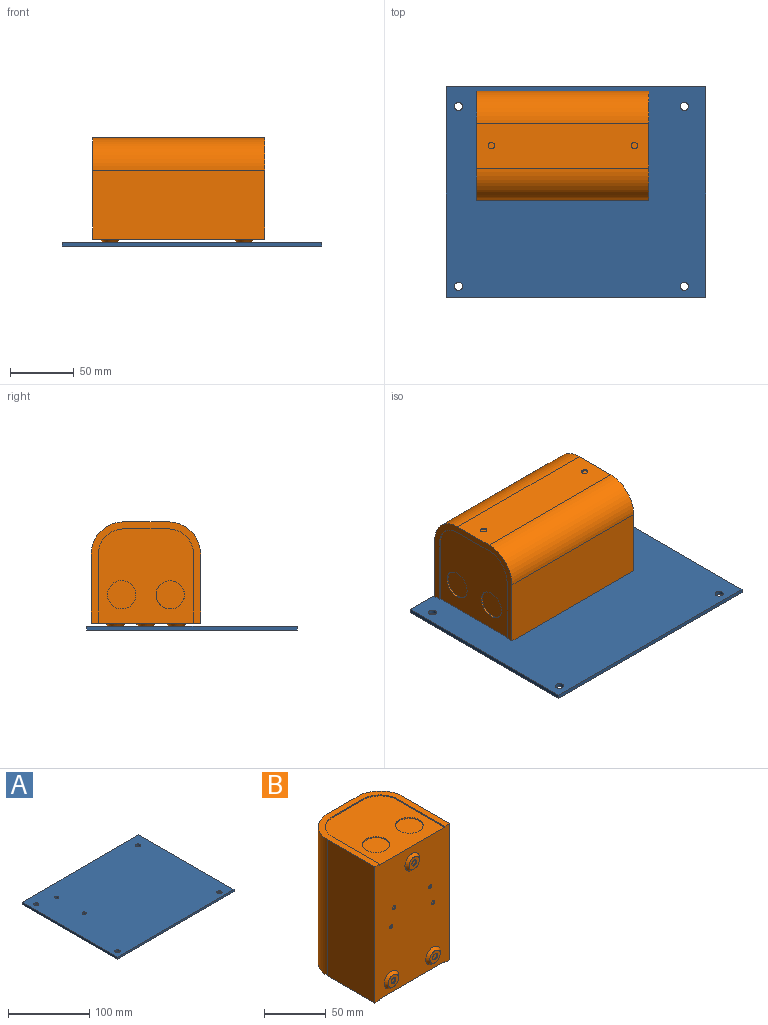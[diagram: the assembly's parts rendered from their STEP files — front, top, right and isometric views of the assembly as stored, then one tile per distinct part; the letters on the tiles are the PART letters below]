
ASSEMBLY  parts=2 mates=1
PART A: 12 faces, bbox 203x165x3.1 mm
  f0: plane 203x3.1mm, normal (0,-1,0), area 629.3mm2, adj f1,f9,f10,f11
  f1: plane 165x3.1mm, normal (1,0,0), area 511.5mm2, adj f0,f2,f10,f11
  f2: plane 203x3.1mm, normal (0,1,0), area 629.3mm2, adj f1,f9,f10,f11
  f3: cylinder r=3.17mm len=6.35mm, axis (0,0,-1), area 61.8mm2, adj f10,f11
  f4: cylinder r=3.17mm len=6.35mm, axis (0,0,-1), area 61.8mm2, adj f10,f11
  f5: cylinder r=3.17mm len=6.35mm, axis (0,0,-1), area 61.8mm2, adj f10,f11
  f6: cylinder r=3.17mm len=6.35mm, axis (0,0,-1), area 61.8mm2, adj f10,f11
  f7: cylinder r=2.5mm len=5mm, axis (0,0,-1), area 48.7mm2, adj f10,f11
  f8: cylinder r=2.5mm len=5mm, axis (0,0,-1), area 48.7mm2, adj f10,f11
  f9: plane 165x3.1mm, normal (-1,0,0), area 511.5mm2, adj f0,f2,f10,f11
  f10: plane 203x165mm, normal (0,0,1), area 33329.1mm2, adj f0,f1,f2,f3,f4,f5,f6,f7
  f11: plane 203x165mm, normal (0,0,-1), area 33329.1mm2, adj f0,f1,f2,f3,f4,f5,f6,f7
PART B: 52 faces, bbox 85.7x81.7x134.9 mm
  f0: plane 85.73x79.38mm, normal (0,0,1), area 1182.2mm2, adj f1,f2,f10,f11,f12,f13,f14,f23
  f1: plane 53.98x1.02mm, normal (-1,0,0), area 54.8mm2, adj f0,f2,f26,f27
  f2: plane 134.93x85.73mm, normal (0,-1,0), area 10735.5mm2, adj f0,f1,f3,f4,f5,f6,f10,f14
  f3: plane 74.68x73.85mm, normal (0,0,-1), area 4569.4mm2, adj f2,f4,f6,f7,f8,f9,f19,f22
  f4: plane 53.98x1.02mm, normal (-1,0,0), area 54.8mm2, adj f2,f3,f5,f9
  f5: plane 85.73x79.38mm, normal (0,0,-1), area 1182.2mm2, adj f2,f4,f6,f7,f8,f9,f10,f11
  f6: plane 53.98x1.02mm, normal (1,0,0), area 54.8mm2, adj f2,f3,f5,f7
  f7: cylinder r=19.88mm len=19.88mm, axis (0,0,-1), area 31.7mm2, adj f3,f5,f6,f8
  f8: plane 34.93x1.02mm, normal (0,-1,0), area 35.5mm2, adj f3,f5,f7,f9
  f9: cylinder r=19.88mm len=19.88mm, axis (0,0,-1), area 31.7mm2, adj f3,f4,f5,f8
  f10: plane 134.93x53.98mm, normal (1,0,0), area 7282.6mm2, adj f0,f2,f5,f11
  f11: cylinder r=25.4mm len=134.93mm, axis (0,0,1), area 5383.3mm2, adj f0,f5,f10,f12
  f12: plane 134.93x34.93mm, normal (0,1,0), area 4671.7mm2, adj f0,f5,f11,f13,f15,f18
  f13: cylinder r=25.4mm len=134.93mm, axis (0,0,1), area 5383.3mm2, adj f0,f5,f12,f14
  f14: plane 134.93x53.98mm, normal (-1,0,0), area 7282.6mm2, adj f0,f2,f5,f13
  f15: cylinder r=2.54mm len=5.08mm, axis (0,1,0), area 16mm2, adj f12,f16
  f16: plane 5.08x5.08mm, normal (0,1,0), area 20.3mm2, adj f15
  f17: plane 5.08x5.08mm, normal (0,1,0), area 20.3mm2, adj f18
  f18: cylinder r=2.54mm len=5.08mm, axis (0,1,0), area 16mm2, adj f12,f17
  f19: cylinder r=11.11mm len=22.23mm, axis (0,0,-1), area 69.8mm2, adj f3,f20
  f20: plane 22.23x22.23mm, normal (0,0,-1), area 387.9mm2, adj f19
  f21: plane 22.23x22.23mm, normal (0,0,-1), area 387.9mm2, adj f22
  f22: cylinder r=11.11mm len=22.23mm, axis (0,0,-1), area 69.8mm2, adj f3,f21
  f23: plane 53.98x1.02mm, normal (1,0,0), area 54.8mm2, adj f0,f2,f24,f27
  f24: cylinder r=19.88mm len=19.88mm, axis (0,0,1), area 31.7mm2, adj f0,f23,f25,f27
  f25: plane 34.93x1.02mm, normal (0,-1,0), area 35.5mm2, adj f0,f24,f26,f27
  f26: cylinder r=19.88mm len=19.88mm, axis (0,0,1), area 31.7mm2, adj f0,f1,f25,f27
  f27: plane 74.68x73.85mm, normal (0,0,1), area 4569.4mm2, adj f1,f2,f23,f24,f25,f26,f28,f31
  f28: cylinder r=11.11mm len=22.23mm, axis (0,0,1), area 69.8mm2, adj f27,f29
  f29: plane 22.23x22.23mm, normal (0,0,1), area 387.9mm2, adj f28
  f30: plane 22.23x22.23mm, normal (0,0,1), area 387.9mm2, adj f31
  f31: cylinder r=11.11mm len=22.23mm, axis (0,0,1), area 69.8mm2, adj f27,f30
  f32: cylinder r=1.71mm len=3.43mm, axis (0,-1,0), area 10.8mm2, adj f2,f33
  f33: plane 3.43x3.43mm, normal (0,-1,0), area 9.2mm2, adj f32
  f34: plane 3.43x3.43mm, normal (0,-1,0), area 9.2mm2, adj f37
  f35: plane 3.43x3.43mm, normal (0,-1,0), area 9.2mm2, adj f38
  f36: plane 3.43x3.43mm, normal (0,-1,0), area 9.2mm2, adj f39
  f37: cylinder r=1.71mm len=3.43mm, axis (0,-1,0), area 10.8mm2, adj f2,f34
  f38: cylinder r=1.71mm len=3.43mm, axis (0,-1,0), area 10.8mm2, adj f2,f35
  f39: cylinder r=1.71mm len=3.43mm, axis (0,-1,0), area 10.8mm2, adj f2,f36
  f40: cone r=7.07mm half-angle=45deg, axis (0,1,0), area 148.5mm2, adj f2,f41
  f41: plane 11.79x11.79mm, normal (0,-1,0), area 85.7mm2, adj f40,f49
  f42: plane 11.79x11.79mm, normal (0,-1,0), area 85.7mm2, adj f48,f50
  f43: plane 11.79x11.79mm, normal (0,-1,0), area 85.7mm2, adj f44,f51
  f44: cylinder r=2.73mm len=5.46mm, axis (0,-1,0), area 17.2mm2, adj f43,f45
  f45: plane 5.46x5.46mm, normal (0,-1,0), area 23.4mm2, adj f44
  f46: plane 5.46x5.46mm, normal (0,-1,0), area 23.4mm2, adj f48
  f47: plane 5.46x5.46mm, normal (0,-1,0), area 23.4mm2, adj f49
  f48: cylinder r=2.73mm len=5.46mm, axis (0,-1,0), area 17.2mm2, adj f42,f46
  f49: cylinder r=2.73mm len=5.46mm, axis (0,-1,0), area 17.2mm2, adj f41,f47
  f50: cone r=7.07mm half-angle=45deg, axis (0,1,0), area 148.5mm2, adj f2,f42
  f51: cone r=7.07mm half-angle=45deg, axis (0,1,0), area 148.5mm2, adj f2,f43
PLACE A t=(-22.99,-13.9,-2.5)mm
PLACE B rot(axis=(0.58,0.58,0.58),120deg) t=(34.22,22.2,2.97)mm
MATE fastened B.f44 <-> A.f7  axis (0,0,-1) through (-86.99,46,0.6)mm
